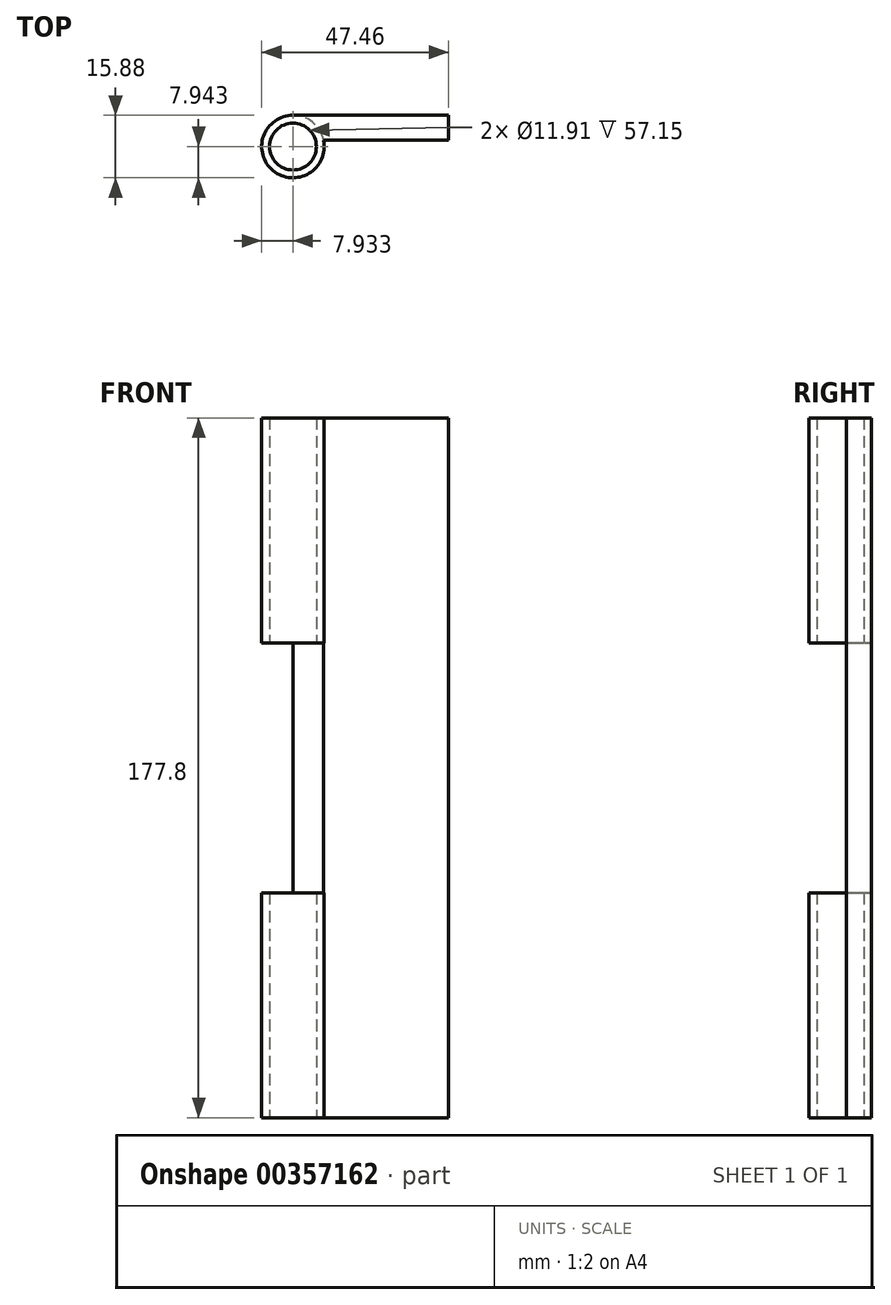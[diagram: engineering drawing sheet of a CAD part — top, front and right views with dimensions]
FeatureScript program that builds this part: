
annotation { "Feature Type Name" : "Feature", "Feature Type Description" : "" }
export const myFeature = defineFeature(function(context is Context, id is Id, definition is map)
    precondition{}
    {
        {
            var Q0;
            Q0=qCreatedBy(makeId("Top.planeOp"),FACE);
            var sketch = newSketch(context, id + "F0", { "sketchPlane" : qUnion([Q0])});
            skLineSegment(sketch, "E0", {"start": v(0, 0) * mm, "end": v(0, -6.35) * mm});
            skLineSegment(sketch, "E1", {"start": v(0, -6.35) * mm, "end": v(-31.75, -6.35) * mm});
            skArc(sketch, "E2", {"start": v(-39.53, 0) * mm, "mid": v(-44.55, -14.09) * mm, "end": v(-31.75, -6.35) * mm});
            skLineSegment(sketch, "E3", {"start": v(-39.53, 0) * mm, "end": v(0, 0) * mm});
            skCircle(sketch, "E4", {"center": v(-39.53, -7.94) * mm, "radius": 5.95 * mm});
            skSolve(sketch);
        }
        {
            var Q0;
            Q0=makeQuery(id+"F0.imprint","IMPRINT",FACE,{"disambiguationData":[TD([[makeQuery(id+"F0.imprint","IMPRINT",EDGE,{"derivedFrom":sQuery(id+"F0.wireOp",EDGE,"E0")}),-1.0]])]});
            extrude(context, id + "F1", {"entities" : qUnion([Q0]), "depth" : 177.8 * mm});
        }
        {
            var Q0;
            Q0=makeQuery(id+"F1.opExtrude","CAP_FACE",FACE,{"disambiguationData":[OSD([sQuery(id+"F0.wireOp",EDGE,"E0"),sQuery(id+"F0.wireOp",EDGE,"E1"),sQuery(id+"F0.wireOp",EDGE,"E2"),sQuery(id+"F0.wireOp",EDGE,"E3"),sQuery(id+"F0.wireOp",EDGE,"E4")])],"isStart":false});
            var Q1;
            Q1=makeQuery(id+"F1.opExtrude","CAP_FACE",FACE,{"disambiguationData":[OSD([sQuery(id+"F0.wireOp",EDGE,"E0"),sQuery(id+"F0.wireOp",EDGE,"E1"),sQuery(id+"F0.wireOp",EDGE,"E2"),sQuery(id+"F0.wireOp",EDGE,"E3"),sQuery(id+"F0.wireOp",EDGE,"E4")])],"isStart":true});
            cPlane(context, id + "F2", {"entities" : qUnion([Q0, Q1]), "cplaneType" : CPlaneType.MID_PLANE, "offset" : 25.4 * mm, "width" : 152.4 * mm, "height" : 152.4 * mm});
        }
        {
            var Q0;
            Q0=qCreatedBy(id+"F2.planeOp",FACE);
            var sketch = newSketch(context, id + "F3", { "sketchPlane" : qUnion([Q0])});
            skCircle(sketch, "E5", {"center": v(-39.53, -7.94) * mm, "radius": 7.94 * mm});
            skSolve(sketch);
        }
        {
            var Q0;
            Q0 = qSketchRegion(id + "F3", true);
            extrude(context, id + "F4", {"entities" : qUnion([Q0]), "operationType" : NewBodyOperationType.REMOVE, "endBound" : BoundingType.SYMMETRIC, "oppositeDirection" : true, "depth" : 63.5 * mm, "hasSecondDirection" : true, "secondDirectionOppositeDirection" : false, "secondDirectionDepth" : 25.4 * mm});
        }
    });
